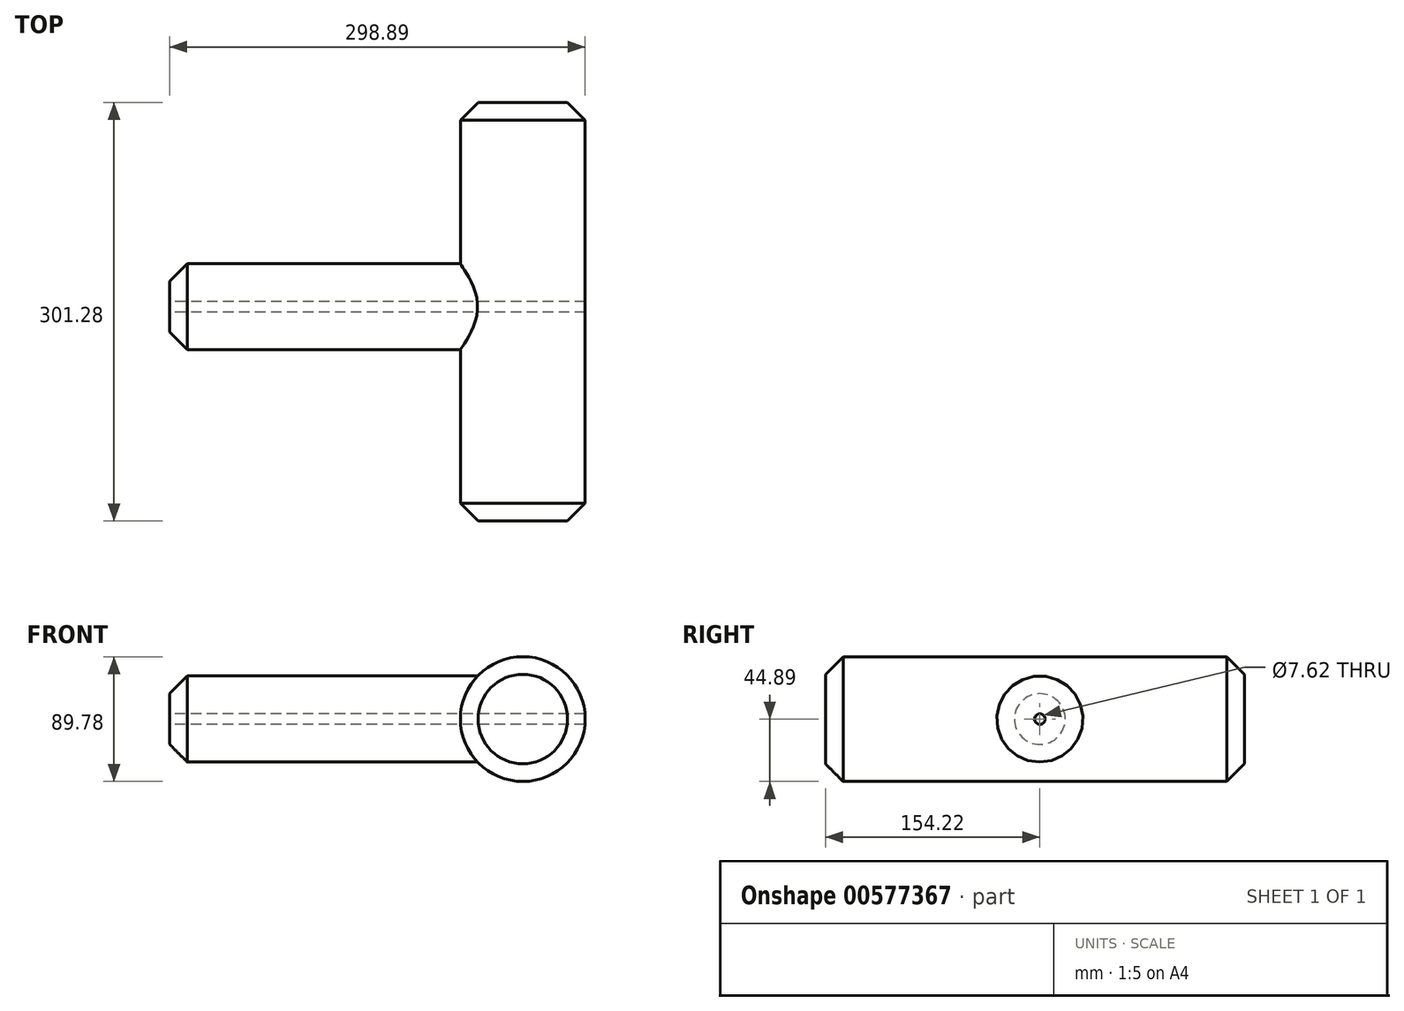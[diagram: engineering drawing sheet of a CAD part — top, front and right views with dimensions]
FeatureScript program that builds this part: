
annotation { "Feature Type Name" : "Feature", "Feature Type Description" : "" }
export const myFeature = defineFeature(function(context is Context, id is Id, definition is map)
    precondition{}
    {
        {
            var Q0;
            Q0=qCreatedBy(makeId("Front.planeOp"),FACE);
            var sketch = newSketch(context, id + "F0", { "sketchPlane" : qUnion([Q0])});
            skCircle(sketch, "E0", {"center": v(0, 0) * mm, "radius": 44.9 * mm});
            skSolve(sketch);
        }
        {
            var Q0;
            Q0=makeQuery(id+"F0.imprint","IMPRINT",FACE,{"disambiguationData":[TD([[makeQuery(id+"F0.imprint","IMPRINT",EDGE,{"derivedFrom":sQuery(id+"F0.wireOp",EDGE,"E0")}),1.0]])]});
            extrude(context, id + "F1", {"entities" : qUnion([Q0]), "depth" : 301.28 * mm, "offsetDistance" : 25.4 * mm});
        }
        {
            var Q0;
            Q0=makeQuery(id+"F1.opExtrude","SWEPT_FACE",FACE,{"disambiguationData":[OSD([sQuery(id+"F0.wireOp",EDGE,"E0")])]});
            chamfer(context, id + "F2", {"entities" : qUnion([Q0]), "width" : 12.7 * mm, "tangentPropagation" : true});
        }
        {
            var Q0;
            Q0=qCreatedBy(makeId("Right.planeOp"),FACE);
            var sketch = newSketch(context, id + "F3", { "sketchPlane" : qUnion([Q0])});
            skCircle(sketch, "E1", {"center": v(-147.06, 0) * mm, "radius": 30.96 * mm});
            skSolve(sketch);
        }
        {
            var Q0;
            Q0 = qSketchRegion(id + "F3", true);
            extrude(context, id + "F4", {"entities" : qUnion([Q0]), "operationType" : NewBodyOperationType.ADD, "oppositeDirection" : true, "depth" : 254 * mm, "offsetDistance" : 25.4 * mm});
        }
        {
            var Q0;
            Q0=makeQuery(id+"F4.opExtrude","CAP_FACE",FACE,{"disambiguationData":[OSD([sQuery(id+"F3.wireOp",EDGE,"E1")])],"isStart":false});
            chamfer(context, id + "F5", {"entities" : qUnion([Q0]), "width" : 12.7 * mm, "tangentPropagation" : true});
        }
        {
            var Q0;
            Q0=makeQuery(id+"F4.opExtrude","CAP_FACE",FACE,{"disambiguationData":[OSD([sQuery(id+"F3.wireOp",EDGE,"E1")])],"isStart":false});
            var sketch = newSketch(context, id + "F6", { "sketchPlane" : qUnion([Q0])});
            skPoint(sketch, "E2", {"position": v(147.06, 0) * mm});
            skSolve(sketch);
        }
        {
            var Q0;
            Q0=sQuery(id+"F6.wireOp",VERTEX,"E2");
            var Q1;
            Q1=makeQuery(id+"F1.opExtrude","SWEPT_BODY",BODY,{"disambiguationData":[OSD([sQuery(id+"F0.wireOp",EDGE,"E0")])]});
            hole(context, id + "F7", {"style" : HoleStyle.SIMPLE, "endStyle" : HoleEndStyle.THROUGH, "holeDiameter" : 7.62 * mm, "isTappedThrough" : true, "tappedDepth" : 12.7 * mm, "tapClearance" : 3, "locations" : qUnion([Q0]), "scope" : qUnion([Q1])});
        }
    });
